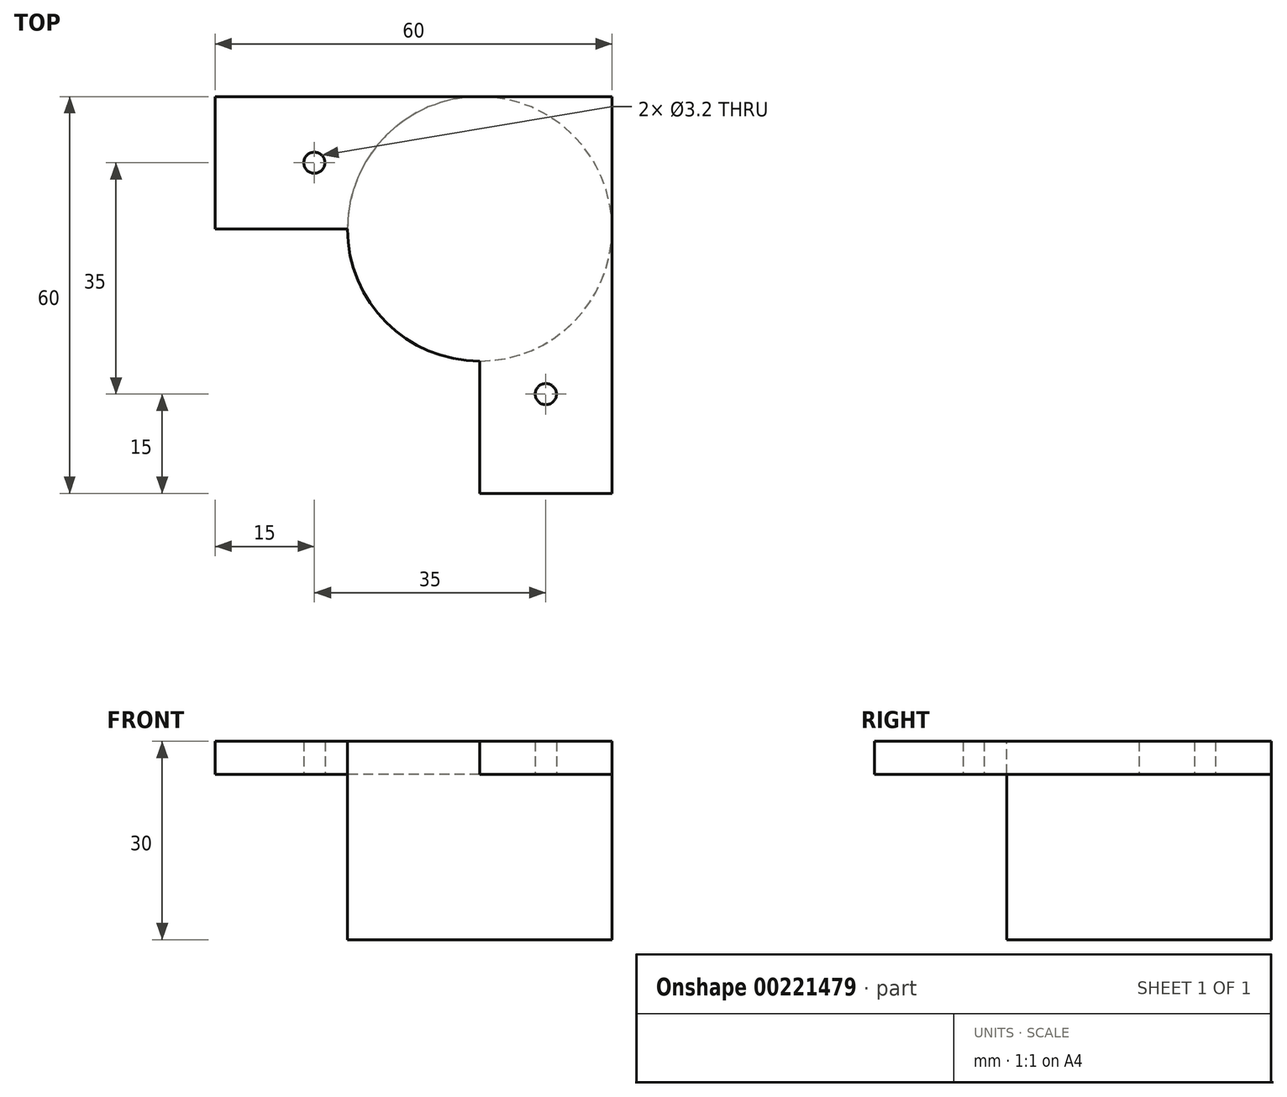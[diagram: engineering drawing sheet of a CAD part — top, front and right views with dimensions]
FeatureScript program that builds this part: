
annotation { "Feature Type Name" : "Feature", "Feature Type Description" : "" }
export const myFeature = defineFeature(function(context is Context, id is Id, definition is map)
    precondition{}
    {
        {
            var Q0;
            Q0=qCreatedBy(makeId("Top.planeOp"),FACE);
            var sketch = newSketch(context, id + "F0", { "sketchPlane" : qUnion([Q0])});
            skLineSegment(sketch, "E0", {"start": v(0, 0) * mm, "end": v(0, 20) * mm});
            skLineSegment(sketch, "E1", {"start": v(0, 20) * mm, "end": v(60, 20) * mm});
            skLineSegment(sketch, "E2", {"start": v(60, 20) * mm, "end": v(60, -40) * mm});
            skLineSegment(sketch, "E3", {"start": v(60, -40) * mm, "end": v(40, -40) * mm});
            skLineSegment(sketch, "E4", {"start": v(40, -40) * mm, "end": v(40, 0) * mm});
            skLineSegment(sketch, "E5", {"start": v(40, 0) * mm, "end": v(0, 0) * mm});
            skSolve(sketch);
        }
        {
            var Q0;
            Q0=makeQuery(id+"F0.imprint","IMPRINT",FACE,{"disambiguationData":[TD([[makeQuery(id+"F0.imprint","IMPRINT",EDGE,{"derivedFrom":sQuery(id+"F0.wireOp",EDGE,"E0")}),-1.0]])]});
            extrude(context, id + "F1", {"entities" : qUnion([Q0]), "depth" : 5 * mm});
        }
        {
            var Q0;
            Q0=makeQuery(id+"F1.opExtrude","CAP_FACE",FACE,{"disambiguationData":[OSD([sQuery(id+"F0.wireOp",EDGE,"E0"),sQuery(id+"F0.wireOp",EDGE,"E1"),sQuery(id+"F0.wireOp",EDGE,"E2"),sQuery(id+"F0.wireOp",EDGE,"E3"),sQuery(id+"F0.wireOp",EDGE,"E4"),sQuery(id+"F0.wireOp",EDGE,"E5")])],"isStart":false});
            var sketch = newSketch(context, id + "F2", { "sketchPlane" : qUnion([Q0])});
            skPoint(sketch, "E6", {"position": v(15, 10) * mm});
            skPoint(sketch, "E6.positionSnap0", {"position": v(0, 10) * mm});
            skPoint(sketch, "E7", {"position": v(50, -25) * mm});
            skPoint(sketch, "E7.positionSnap0", {"position": v(50, -40) * mm});
            skSolve(sketch);
        }
        {
            var Q0;
            Q0=sQuery(id+"F2.wireOp",VERTEX,"E6");
            var Q1;
            Q1=sQuery(id+"F2.wireOp",VERTEX,"E7");
            var Q2;
            Q2=makeQuery(id+"F1.opExtrude","SWEPT_BODY",BODY,{"disambiguationData":[OSD([sQuery(id+"F0.wireOp",EDGE,"E0"),sQuery(id+"F0.wireOp",EDGE,"E1"),sQuery(id+"F0.wireOp",EDGE,"E2"),sQuery(id+"F0.wireOp",EDGE,"E3"),sQuery(id+"F0.wireOp",EDGE,"E4"),sQuery(id+"F0.wireOp",EDGE,"E5")])]});
            hole(context, id + "F3", {"style" : HoleStyle.SIMPLE, "endStyle" : HoleEndStyle.THROUGH, "holeDiameter" : 3.2 * mm, "locations" : qUnion([Q0, Q1]), "scope" : qUnion([Q2]), "isTappedThrough" : true});
        }
        {
            var Q0;
            Q0=makeQuery(id+"F1.opExtrude","CAP_FACE",FACE,{"disambiguationData":[OSD([sQuery(id+"F0.wireOp",EDGE,"E0"),sQuery(id+"F0.wireOp",EDGE,"E1"),sQuery(id+"F0.wireOp",EDGE,"E2"),sQuery(id+"F0.wireOp",EDGE,"E3"),sQuery(id+"F0.wireOp",EDGE,"E4"),sQuery(id+"F0.wireOp",EDGE,"E5")])],"isStart":false});
            var sketch = newSketch(context, id + "F4", { "sketchPlane" : qUnion([Q0])});
            skCircle(sketch, "E8", {"center": v(40, 0) * mm, "radius": 20 * mm});
            skSolve(sketch);
        }
        {
            var Q0;
            {var subQ3=sQuery(id+"F4.wireOp",EDGE,"E8");var subQ6=makeQuery(id+"F4.imprint","INTERSECT",VERTEX,{"derivedFrom":[makeQuery(id+"F1.opExtrude","CAP_EDGE",EDGE,{"disambiguationData":[OSD([sQuery(id+"F0.wireOp",EDGE,"E1")])],"isStart":false}),subQ3]});Q0=makeQuery(id+"F4.imprint","IMPRINT",FACE,{"disambiguationData":[TD([[makeQuery(id+"F4.imprint","IMPRINT",EDGE,{"disambiguationData":[TD([[subQ6,1.0]])],"derivedFrom":subQ3}),1.0]])]});}
            var Q1;
            {var subQ0=sQuery(id+"F4.wireOp",EDGE,"E8");var subQ1=makeQuery(id+"F1.opExtrude","CAP_EDGE",EDGE,{"disambiguationData":[OSD([sQuery(id+"F0.wireOp",EDGE,"E5")])],"isStart":false});var subQ2=makeQuery(id+"F4.imprint","INTERSECT",VERTEX,{"derivedFrom":[subQ1,subQ0]});Q1=makeQuery(id+"F4.imprint","IMPRINT",FACE,{"disambiguationData":[TD([[makeQuery(id+"F4.imprint","IMPRINT",EDGE,{"disambiguationData":[TD([[subQ2,-1.0]])],"derivedFrom":subQ0}),1.0]])]});}
            extrude(context, id + "F5", {"entities" : qUnion([Q0, Q1]), "operationType" : NewBodyOperationType.ADD, "oppositeDirection" : true, "depth" : 30 * mm});
        }
    });
